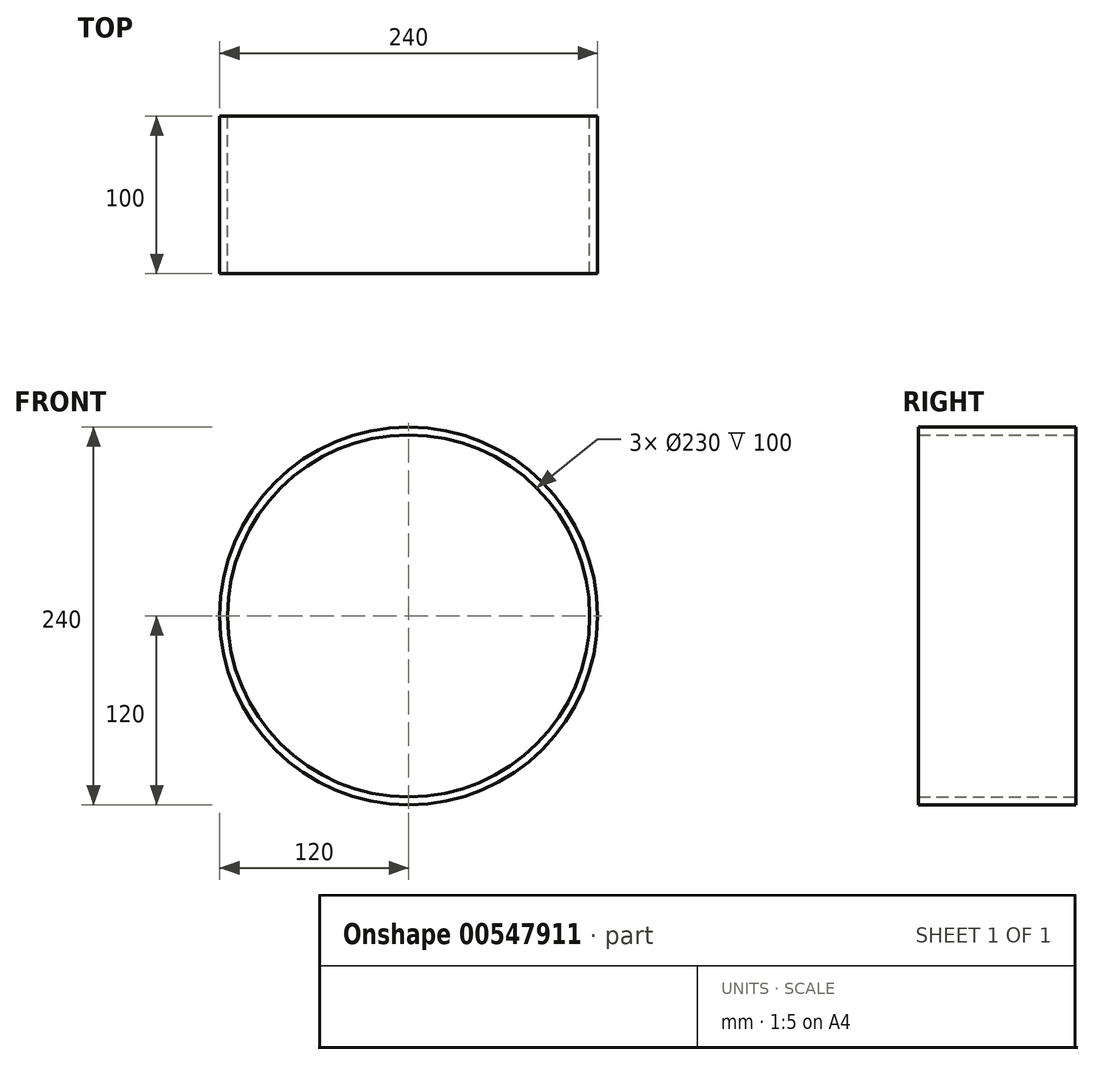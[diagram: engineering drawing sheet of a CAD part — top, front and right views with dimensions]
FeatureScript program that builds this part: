
annotation { "Feature Type Name" : "Feature", "Feature Type Description" : "" }
export const myFeature = defineFeature(function(context is Context, id is Id, definition is map)
    precondition{}
    {
        {
            var Q0;
            Q0=qCreatedBy(makeId("Front.planeOp"),FACE);
            var sketch = newSketch(context, id + "F0", { "sketchPlane" : qUnion([Q0])});
            skCircle(sketch, "E0", {"center": v(0, 0) * mm, "radius": 120 * mm});
            skCircle(sketch, "E1", {"center": v(0, 0) * mm, "radius": 115 * mm});
            skSolve(sketch);
        }
        {
            var Q0;
            Q0 = qSketchRegion(id + "F0", true);
            extrude(context, id + "F1", {"entities" : qUnion([Q0]), "endBound" : BoundingType.SYMMETRIC, "depth" : 100 * mm, "offsetDistance" : 25 * mm});
        }
    });
